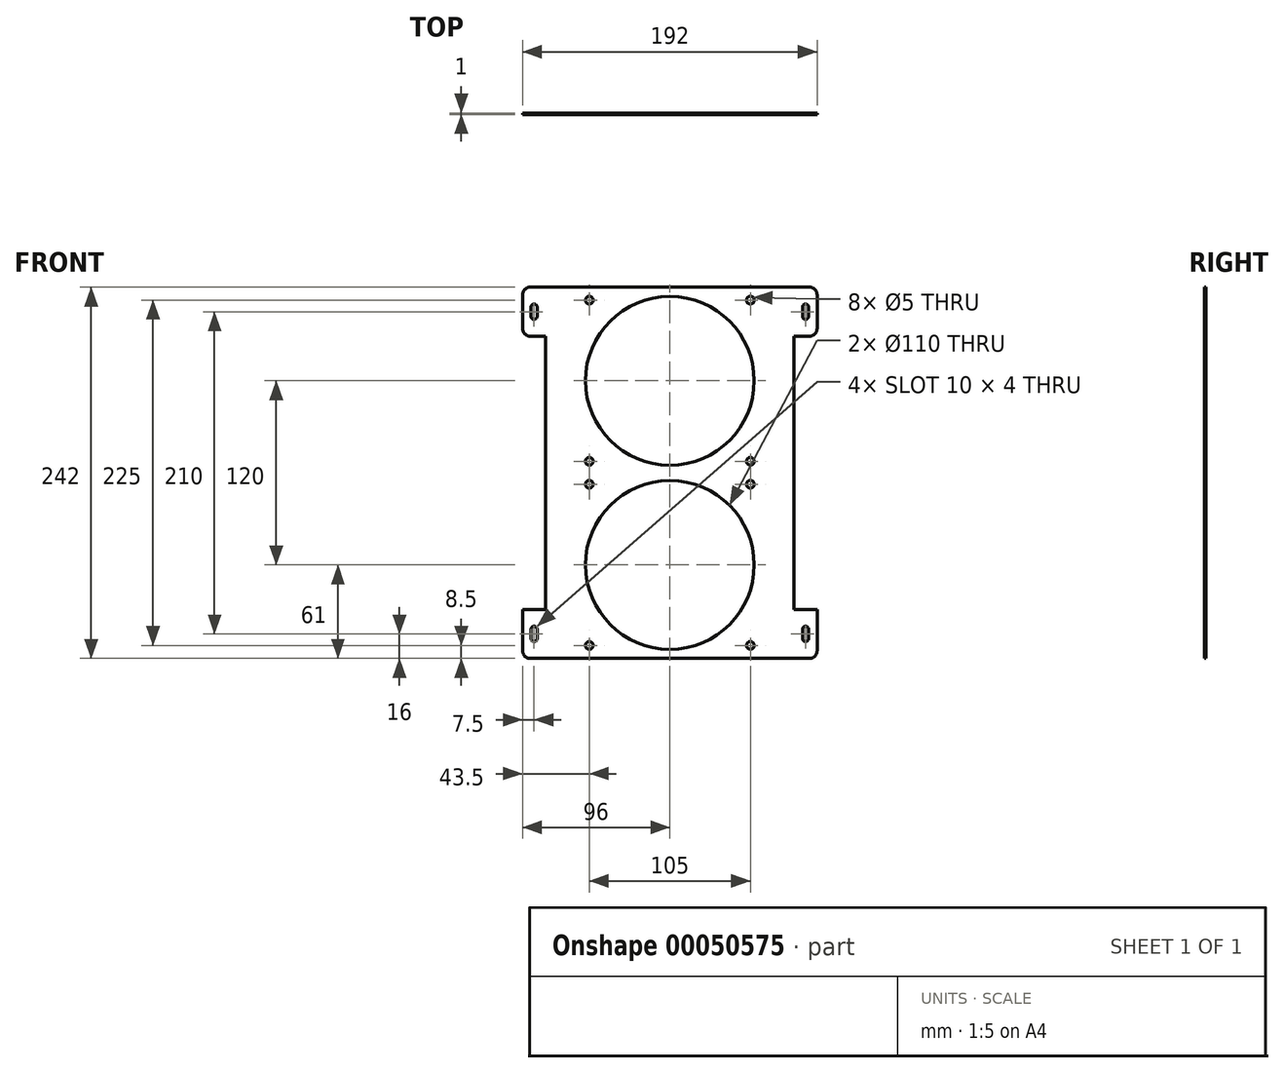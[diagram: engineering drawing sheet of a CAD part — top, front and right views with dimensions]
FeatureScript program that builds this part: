
annotation { "Feature Type Name" : "Feature", "Feature Type Description" : "" }
export const myFeature = defineFeature(function(context is Context, id is Id, definition is map)
    precondition{}
    {
        {
            var Q0;
            Q0=qCreatedBy(makeId("Front.planeOp"),FACE);
            var sketch = newSketch(context, id + "F0", { "sketchPlane" : qUnion([Q0])});
            skLineSegment(sketch, "E0.bottom", {"start": v(0, 0) * mm, "end": v(192, 0) * mm});
            skLineSegment(sketch, "E0.top", {"start": v(0, 242) * mm, "end": v(192, 242) * mm});
            skLineSegment(sketch, "E0.left", {"start": v(0, 0) * mm, "end": v(0, 242) * mm});
            skLineSegment(sketch, "E0.right", {"start": v(192, 0) * mm, "end": v(192, 242) * mm});
            skSolve(sketch);
        }
        {
            var Q0;
            Q0=makeQuery(id+"F0.imprint","IMPRINT",FACE,{"disambiguationData":[TD([[makeQuery(id+"F0.imprint","IMPRINT",EDGE,{"derivedFrom":sQuery(id+"F0.wireOp",EDGE,"E0.bottom")}),1.0]])]});
            extrude(context, id + "F1", {"entities" : qUnion([Q0]), "depth" : 1 * mm});
        }
        {
            var Q0;
            Q0=makeQuery(id+"F1.opExtrude","CAP_FACE",FACE,{"disambiguationData":[OSD([sQuery(id+"F0.wireOp",EDGE,"E0.bottom"),sQuery(id+"F0.wireOp",EDGE,"E0.top"),sQuery(id+"F0.wireOp",EDGE,"E0.left"),sQuery(id+"F0.wireOp",EDGE,"E0.right")])],"isStart":false});
            var sketch = newSketch(context, id + "F2", { "sketchPlane" : qUnion([Q0])});
            skCircle(sketch, "E1", {"center": v(96, 181) * mm, "radius": 55 * mm});
            skCircle(sketch, "E2", {"center": v(96, 61) * mm, "radius": 55 * mm});
            skSolve(sketch);
        }
        {
            var Q0;
            Q0=sQuery(id+"F2.wireOp",VERTEX,"E1.center");
            var Q1;
            Q1=sQuery(id+"F2.wireOp",VERTEX,"E2.center");
            var Q2;
            Q2=makeQuery(id+"F1.opExtrude","SWEPT_BODY",BODY,{"disambiguationData":[OSD([sQuery(id+"F0.wireOp",EDGE,"E0.bottom"),sQuery(id+"F0.wireOp",EDGE,"E0.top"),sQuery(id+"F0.wireOp",EDGE,"E0.left"),sQuery(id+"F0.wireOp",EDGE,"E0.right")])]});
            hole(context, id + "F3", {"style" : HoleStyle.SIMPLE, "holeDiameter" : 110 * mm, "endStyle" : HoleEndStyle.THROUGH, "locations" : qUnion([Q0, Q1]), "scope" : qUnion([Q2])});
        }
        {
            var Q0;
            Q0=makeQuery(id+"F1.opExtrude","CAP_FACE",FACE,{"disambiguationData":[OSD([sQuery(id+"F0.wireOp",EDGE,"E0.bottom"),sQuery(id+"F0.wireOp",EDGE,"E0.top"),sQuery(id+"F0.wireOp",EDGE,"E0.left"),sQuery(id+"F0.wireOp",EDGE,"E0.right")])],"isStart":false});
            var sketch = newSketch(context, id + "F4", { "sketchPlane" : qUnion([Q0])});
            skLineSegment(sketch, "E3", {"start": v(43.5, 242) * mm, "end": v(43.5, 0) * mm, "construction": true});
            skLineSegment(sketch, "E4", {"start": v(148.5, 242) * mm, "end": v(148.5, 0) * mm, "construction": true});
            skLineSegment(sketch, "E5", {"start": v(0, 128.5) * mm, "end": v(192, 128.5) * mm, "construction": true});
            skLineSegment(sketch, "E6", {"start": v(0, 113.5) * mm, "end": v(192, 113.5) * mm, "construction": true});
            skLineSegment(sketch, "E7", {"start": v(0, 8.5) * mm, "end": v(192, 8.5) * mm, "construction": true});
            skLineSegment(sketch, "E8", {"start": v(0, 233.5) * mm, "end": v(192, 233.5) * mm, "construction": true});
            skLineSegment(sketch, "E9", {"start": v(96, 242) * mm, "end": v(96, 0) * mm, "construction": true});
            skLineSegment(sketch, "E10", {"start": v(0, 181) * mm, "end": v(192, 181) * mm, "construction": true});
            skLineSegment(sketch, "E11", {"start": v(0, 61) * mm, "end": v(192, 61) * mm, "construction": true});
            skPoint(sketch, "E12", {"position": v(43.5, 233.5) * mm});
            skPoint(sketch, "E13", {"position": v(148.5, 233.5) * mm});
            skPoint(sketch, "E14", {"position": v(43.5, 128.5) * mm});
            skPoint(sketch, "E15", {"position": v(148.5, 128.5) * mm});
            skPoint(sketch, "E16", {"position": v(43.5, 113.5) * mm});
            skPoint(sketch, "E17", {"position": v(148.5, 113.5) * mm});
            skPoint(sketch, "E18", {"position": v(148.5, 8.5) * mm});
            skPoint(sketch, "E19", {"position": v(43.5, 8.5) * mm});
            skSolve(sketch);
        }
        {
            var Q0;
            Q0=sQuery(id+"F4.wireOp",VERTEX,"E12");
            var Q1;
            Q1=sQuery(id+"F4.wireOp",VERTEX,"E13");
            var Q2;
            Q2=sQuery(id+"F4.wireOp",VERTEX,"E14");
            var Q3;
            Q3=sQuery(id+"F4.wireOp",VERTEX,"E15");
            var Q4;
            Q4=sQuery(id+"F4.wireOp",VERTEX,"E16");
            var Q5;
            Q5=sQuery(id+"F4.wireOp",VERTEX,"E17");
            var Q6;
            Q6=sQuery(id+"F4.wireOp",VERTEX,"E19");
            var Q7;
            Q7=sQuery(id+"F4.wireOp",VERTEX,"E18");
            var Q8;
            Q8=makeQuery(id+"F1.opExtrude","SWEPT_BODY",BODY,{"disambiguationData":[OSD([sQuery(id+"F0.wireOp",EDGE,"E0.bottom"),sQuery(id+"F0.wireOp",EDGE,"E0.top"),sQuery(id+"F0.wireOp",EDGE,"E0.left"),sQuery(id+"F0.wireOp",EDGE,"E0.right")])]});
            hole(context, id + "F5", {"style" : HoleStyle.SIMPLE, "holeDiameter" : 5 * mm, "endStyle" : HoleEndStyle.THROUGH, "locations" : qUnion([Q0, Q1, Q2, Q3, Q4, Q5, Q6, Q7]), "scope" : qUnion([Q8])});
        }
        {
            var Q0;
            Q0=makeQuery(id+"F1.opExtrude","CAP_FACE",FACE,{"disambiguationData":[OSD([sQuery(id+"F0.wireOp",EDGE,"E0.bottom"),sQuery(id+"F0.wireOp",EDGE,"E0.top"),sQuery(id+"F0.wireOp",EDGE,"E0.left"),sQuery(id+"F0.wireOp",EDGE,"E0.right")])],"isStart":false});
            var sketch = newSketch(context, id + "F6", { "sketchPlane" : qUnion([Q0])});
            skLineSegment(sketch, "E20", {"start": v(0, 210) * mm, "end": v(15, 210) * mm});
            skLineSegment(sketch, "E21", {"start": v(15, 210) * mm, "end": v(15, 32) * mm});
            skLineSegment(sketch, "E22", {"start": v(15, 32) * mm, "end": v(0, 32) * mm});
            skLineSegment(sketch, "E23", {"start": v(192, 210) * mm, "end": v(177, 210) * mm});
            skLineSegment(sketch, "E24", {"start": v(177, 210) * mm, "end": v(177, 32) * mm});
            skLineSegment(sketch, "E25", {"start": v(177, 32) * mm, "end": v(192, 32) * mm});
            skLineSegment(sketch, "E26", {"start": v(192, 32) * mm, "end": v(192, 210) * mm});
            skLineSegment(sketch, "E27", {"start": v(0, 210) * mm, "end": v(0, 32) * mm});
            skSolve(sketch);
        }
        {
            var Q0;
            Q0=makeQuery(id+"F6.imprint","IMPRINT",FACE,{"disambiguationData":[TD([[makeQuery(id+"F6.imprint","IMPRINT",EDGE,{"derivedFrom":sQuery(id+"F6.wireOp",EDGE,"E20")}),-1.0]])]});
            var Q1;
            Q1=makeQuery(id+"F6.imprint","IMPRINT",FACE,{"disambiguationData":[TD([[makeQuery(id+"F6.imprint","IMPRINT",EDGE,{"derivedFrom":sQuery(id+"F6.wireOp",EDGE,"E23")}),1.0]])]});
            extrude(context, id + "F7", {"entities" : qUnion([Q0, Q1]), "operationType" : NewBodyOperationType.REMOVE, "oppositeDirection" : true, "depth" : 1 * mm});
        }
        {
            var Q0;
            Q0=makeQuery(id+"F7.boolean.opBoolean","COPY",EDGE,{"derivedFrom":makeQuery(id+"F7.opExtrude","SWEPT_EDGE",EDGE,{"disambiguationData":[OSD([sQuery(id+"F0.wireOp",EDGE,"E0.left"),sQuery(id+"F6.wireOp",EDGE,"E20"),sQuery(id+"F6.wireOp",EDGE,"E27")])]})});
            var Q1;
            Q1=makeQuery(id+"F1.opExtrude","SWEPT_EDGE",EDGE,{"disambiguationData":[OSD([sQuery(id+"F0.wireOp",EDGE,"E0.top"),sQuery(id+"F0.wireOp",EDGE,"E0.left")])]});
            var Q2;
            Q2=makeQuery(id+"F7.boolean.opBoolean","COPY",EDGE,{"derivedFrom":makeQuery(id+"F7.opExtrude","SWEPT_EDGE",EDGE,{"disambiguationData":[OSD([sQuery(id+"F0.wireOp",EDGE,"E0.left"),sQuery(id+"F6.wireOp",EDGE,"E22"),sQuery(id+"F6.wireOp",EDGE,"E27")])]})});
            var Q3;
            Q3=makeQuery(id+"F1.opExtrude","SWEPT_EDGE",EDGE,{"disambiguationData":[OSD([sQuery(id+"F0.wireOp",EDGE,"E0.bottom"),sQuery(id+"F0.wireOp",EDGE,"E0.left")])]});
            var Q4;
            Q4=makeQuery(id+"F7.boolean.opBoolean","COPY",EDGE,{"derivedFrom":makeQuery(id+"F7.opExtrude","SWEPT_EDGE",EDGE,{"disambiguationData":[OSD([sQuery(id+"F0.wireOp",EDGE,"E0.right"),sQuery(id+"F6.wireOp",EDGE,"E25"),sQuery(id+"F6.wireOp",EDGE,"E26")])]})});
            var Q5;
            Q5=makeQuery(id+"F1.opExtrude","SWEPT_EDGE",EDGE,{"disambiguationData":[OSD([sQuery(id+"F0.wireOp",EDGE,"E0.bottom"),sQuery(id+"F0.wireOp",EDGE,"E0.right")])]});
            var Q6;
            Q6=makeQuery(id+"F1.opExtrude","SWEPT_EDGE",EDGE,{"disambiguationData":[OSD([sQuery(id+"F0.wireOp",EDGE,"E0.top"),sQuery(id+"F0.wireOp",EDGE,"E0.right")])]});
            var Q7;
            Q7=makeQuery(id+"F7.boolean.opBoolean","COPY",EDGE,{"derivedFrom":makeQuery(id+"F7.opExtrude","SWEPT_EDGE",EDGE,{"disambiguationData":[OSD([sQuery(id+"F0.wireOp",EDGE,"E0.right"),sQuery(id+"F6.wireOp",EDGE,"E23"),sQuery(id+"F6.wireOp",EDGE,"E26")])]})});
            fillet(context, id + "F8", {"entities" : qUnion([Q0, Q1, Q2, Q3, Q4, Q5, Q6, Q7]), "radius" : 5 * mm, "tangentPropagation" : true, "allowEdgeOverflow" : false});
        }
        {
            var Q0;
            Q0=makeQuery(id+"F1.opExtrude","CAP_FACE",FACE,{"disambiguationData":[OSD([sQuery(id+"F0.wireOp",EDGE,"E0.bottom"),sQuery(id+"F0.wireOp",EDGE,"E0.top"),sQuery(id+"F0.wireOp",EDGE,"E0.left"),sQuery(id+"F0.wireOp",EDGE,"E0.right")])],"isStart":false});
            var sketch = newSketch(context, id + "F9", { "sketchPlane" : qUnion([Q0])});
            skLineSegment(sketch, "E28.bottom", {"start": v(5.5, 231) * mm, "end": v(9.5, 231) * mm});
            skLineSegment(sketch, "E28.top", {"start": v(5.5, 221) * mm, "end": v(9.5, 221) * mm});
            skLineSegment(sketch, "E28.left", {"start": v(5.5, 231) * mm, "end": v(5.5, 221) * mm});
            skLineSegment(sketch, "E28.right", {"start": v(9.5, 231) * mm, "end": v(9.5, 221) * mm});
            skLineSegment(sketch, "E29.bottom", {"start": v(182.5, 231) * mm, "end": v(186.5, 231) * mm});
            skLineSegment(sketch, "E29.top", {"start": v(182.5, 221) * mm, "end": v(186.5, 221) * mm});
            skLineSegment(sketch, "E29.left", {"start": v(182.5, 231) * mm, "end": v(182.5, 221) * mm});
            skLineSegment(sketch, "E29.right", {"start": v(186.5, 231) * mm, "end": v(186.5, 221) * mm});
            skLineSegment(sketch, "E30.bottom", {"start": v(5.5, 21) * mm, "end": v(9.5, 21) * mm});
            skLineSegment(sketch, "E30.top", {"start": v(5.5, 11) * mm, "end": v(9.5, 11) * mm});
            skLineSegment(sketch, "E30.left", {"start": v(5.5, 21) * mm, "end": v(5.5, 11) * mm});
            skLineSegment(sketch, "E30.right", {"start": v(9.5, 21) * mm, "end": v(9.5, 11) * mm});
            skLineSegment(sketch, "E31.bottom", {"start": v(182.5, 21) * mm, "end": v(186.5, 21) * mm});
            skLineSegment(sketch, "E31.top", {"start": v(182.5, 11) * mm, "end": v(186.5, 11) * mm});
            skLineSegment(sketch, "E31.left", {"start": v(182.5, 21) * mm, "end": v(182.5, 11) * mm});
            skLineSegment(sketch, "E31.right", {"start": v(186.5, 21) * mm, "end": v(186.5, 11) * mm});
            skSolve(sketch);
        }
        {
            var Q0;
            Q0 = qSketchRegion(id + "F9", true);
            extrude(context, id + "F10", {"entities" : qUnion([Q0]), "operationType" : NewBodyOperationType.REMOVE, "oppositeDirection" : true, "depth" : 1 * mm});
        }
        {
            var Q0;
            Q0=makeQuery(id+"F10.boolean.opBoolean","COPY",EDGE,{"derivedFrom":makeQuery(id+"F10.opExtrude","SWEPT_EDGE",EDGE,{"disambiguationData":[OSD([sQuery(id+"F9.wireOp",EDGE,"E28.bottom"),sQuery(id+"F9.wireOp",EDGE,"E28.right")])]})});
            var Q1;
            Q1=makeQuery(id+"F10.boolean.opBoolean","COPY",EDGE,{"derivedFrom":makeQuery(id+"F10.opExtrude","SWEPT_EDGE",EDGE,{"disambiguationData":[OSD([sQuery(id+"F9.wireOp",EDGE,"E28.bottom"),sQuery(id+"F9.wireOp",EDGE,"E28.left")])]})});
            var Q2;
            Q2=makeQuery(id+"F10.boolean.opBoolean","COPY",EDGE,{"derivedFrom":makeQuery(id+"F10.opExtrude","SWEPT_EDGE",EDGE,{"disambiguationData":[OSD([sQuery(id+"F9.wireOp",EDGE,"E28.top"),sQuery(id+"F9.wireOp",EDGE,"E28.left")])]})});
            var Q3;
            Q3=makeQuery(id+"F10.boolean.opBoolean","COPY",EDGE,{"derivedFrom":makeQuery(id+"F10.opExtrude","SWEPT_EDGE",EDGE,{"disambiguationData":[OSD([sQuery(id+"F9.wireOp",EDGE,"E28.top"),sQuery(id+"F9.wireOp",EDGE,"E28.right")])]})});
            var Q4;
            Q4=makeQuery(id+"F10.boolean.opBoolean","COPY",EDGE,{"derivedFrom":makeQuery(id+"F10.opExtrude","SWEPT_EDGE",EDGE,{"disambiguationData":[OSD([sQuery(id+"F9.wireOp",EDGE,"E29.bottom"),sQuery(id+"F9.wireOp",EDGE,"E29.left")])]})});
            var Q5;
            Q5=makeQuery(id+"F10.boolean.opBoolean","COPY",EDGE,{"derivedFrom":makeQuery(id+"F10.opExtrude","SWEPT_EDGE",EDGE,{"disambiguationData":[OSD([sQuery(id+"F9.wireOp",EDGE,"E29.bottom"),sQuery(id+"F9.wireOp",EDGE,"E29.right")])]})});
            var Q6;
            Q6=makeQuery(id+"F10.boolean.opBoolean","COPY",EDGE,{"derivedFrom":makeQuery(id+"F10.opExtrude","SWEPT_EDGE",EDGE,{"disambiguationData":[OSD([sQuery(id+"F9.wireOp",EDGE,"E29.top"),sQuery(id+"F9.wireOp",EDGE,"E29.left")])]})});
            var Q7;
            Q7=makeQuery(id+"F10.boolean.opBoolean","COPY",EDGE,{"derivedFrom":makeQuery(id+"F10.opExtrude","SWEPT_EDGE",EDGE,{"disambiguationData":[OSD([sQuery(id+"F9.wireOp",EDGE,"E29.top"),sQuery(id+"F9.wireOp",EDGE,"E29.right")])]})});
            var Q8;
            Q8=makeQuery(id+"F10.boolean.opBoolean","COPY",EDGE,{"derivedFrom":makeQuery(id+"F10.opExtrude","SWEPT_EDGE",EDGE,{"disambiguationData":[OSD([sQuery(id+"F9.wireOp",EDGE,"E31.bottom"),sQuery(id+"F9.wireOp",EDGE,"E31.left")])]})});
            var Q9;
            Q9=makeQuery(id+"F10.boolean.opBoolean","COPY",EDGE,{"derivedFrom":makeQuery(id+"F10.opExtrude","SWEPT_EDGE",EDGE,{"disambiguationData":[OSD([sQuery(id+"F9.wireOp",EDGE,"E31.bottom"),sQuery(id+"F9.wireOp",EDGE,"E31.right")])]})});
            var Q10;
            Q10=makeQuery(id+"F10.boolean.opBoolean","COPY",EDGE,{"derivedFrom":makeQuery(id+"F10.opExtrude","SWEPT_EDGE",EDGE,{"disambiguationData":[OSD([sQuery(id+"F9.wireOp",EDGE,"E31.top"),sQuery(id+"F9.wireOp",EDGE,"E31.right")])]})});
            var Q11;
            Q11=makeQuery(id+"F10.boolean.opBoolean","COPY",EDGE,{"derivedFrom":makeQuery(id+"F10.opExtrude","SWEPT_EDGE",EDGE,{"disambiguationData":[OSD([sQuery(id+"F9.wireOp",EDGE,"E31.top"),sQuery(id+"F9.wireOp",EDGE,"E31.left")])]})});
            var Q12;
            Q12=makeQuery(id+"F10.boolean.opBoolean","COPY",EDGE,{"derivedFrom":makeQuery(id+"F10.opExtrude","SWEPT_EDGE",EDGE,{"disambiguationData":[OSD([sQuery(id+"F9.wireOp",EDGE,"E30.bottom"),sQuery(id+"F9.wireOp",EDGE,"E30.left")])]})});
            var Q13;
            Q13=makeQuery(id+"F10.boolean.opBoolean","COPY",EDGE,{"derivedFrom":makeQuery(id+"F10.opExtrude","SWEPT_EDGE",EDGE,{"disambiguationData":[OSD([sQuery(id+"F9.wireOp",EDGE,"E30.bottom"),sQuery(id+"F9.wireOp",EDGE,"E30.right")])]})});
            var Q14;
            Q14=makeQuery(id+"F10.boolean.opBoolean","COPY",EDGE,{"derivedFrom":makeQuery(id+"F10.opExtrude","SWEPT_EDGE",EDGE,{"disambiguationData":[OSD([sQuery(id+"F9.wireOp",EDGE,"E30.top"),sQuery(id+"F9.wireOp",EDGE,"E30.right")])]})});
            var Q15;
            Q15=makeQuery(id+"F10.boolean.opBoolean","COPY",EDGE,{"derivedFrom":makeQuery(id+"F10.opExtrude","SWEPT_EDGE",EDGE,{"disambiguationData":[OSD([sQuery(id+"F9.wireOp",EDGE,"E30.top"),sQuery(id+"F9.wireOp",EDGE,"E30.left")])]})});
            fillet(context, id + "F11", {"entities" : qUnion([Q0, Q1, Q2, Q3, Q4, Q5, Q6, Q7, Q8, Q9, Q10, Q11, Q12, Q13, Q14, Q15]), "radius" : 2 * mm, "tangentPropagation" : true, "allowEdgeOverflow" : false});
        }
    });
